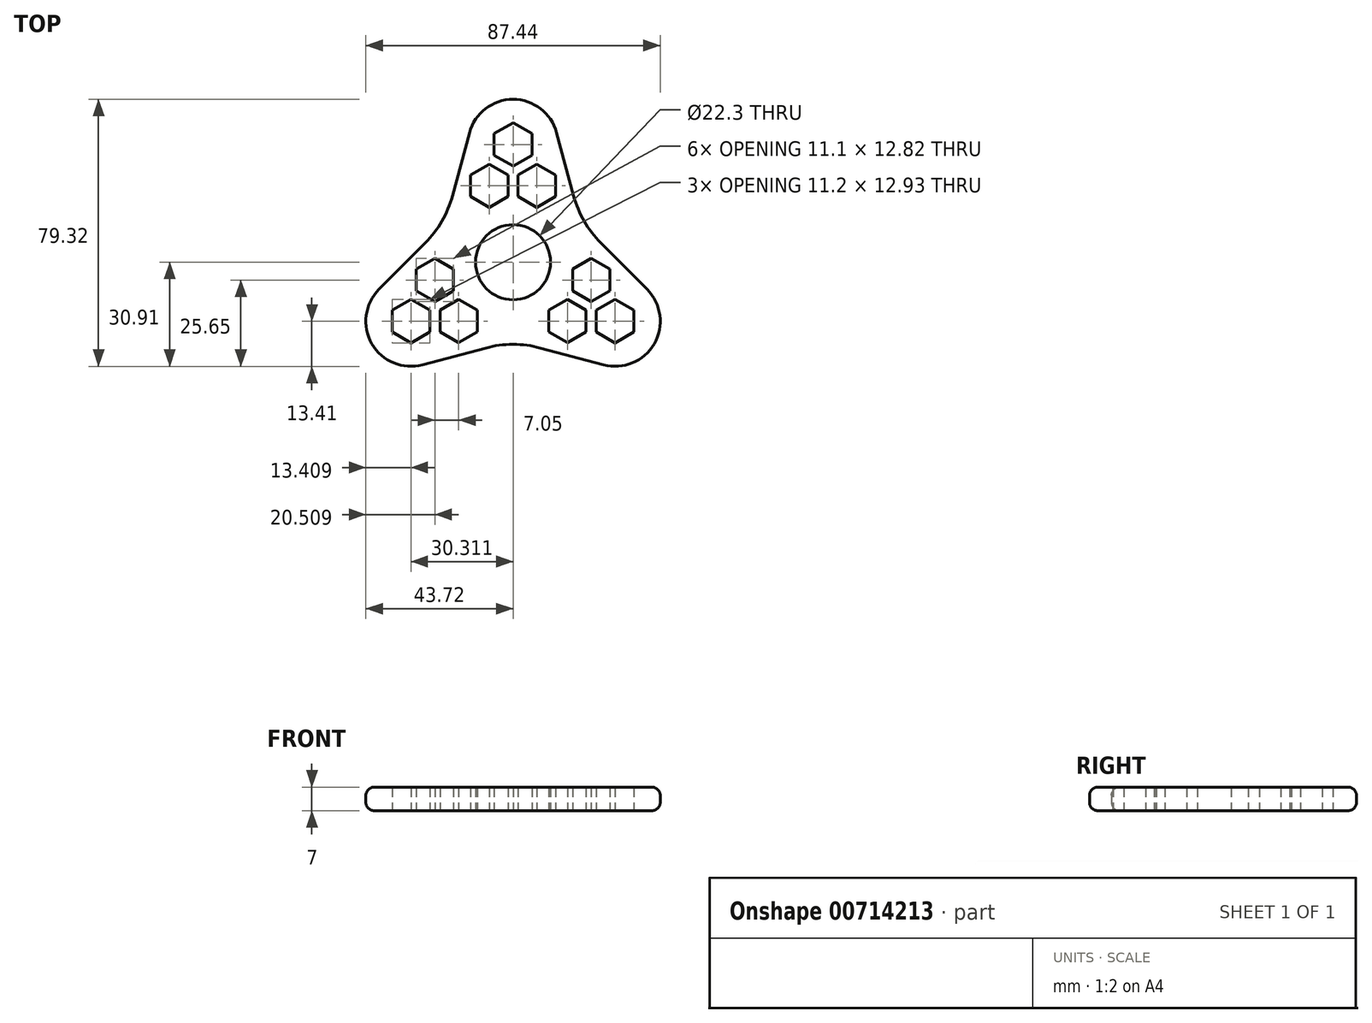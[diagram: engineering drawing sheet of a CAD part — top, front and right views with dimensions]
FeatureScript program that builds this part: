
annotation { "Feature Type Name" : "Feature", "Feature Type Description" : "" }
export const myFeature = defineFeature(function(context is Context, id is Id, definition is map)
    precondition{}
    {
        {
            var Q0;
            Q0=qCreatedBy(makeId("Top.planeOp"),FACE);
            var sketch = newSketch(context, id + "F0", { "sketchPlane" : qUnion([Q0])});
            skCircle(sketch, "E0", {"center": v(0, 0) * mm, "radius": 11.15 * mm});
            skCircle(sketch, "E1.cCircle", {"center": v(0, 35) * mm, "radius": 5.6 * mm, "construction": true});
            skLineSegment(sketch, "E1.0", {"start": v(5.6, 38.23) * mm, "end": v(5.6, 31.77) * mm});
            skLineSegment(sketch, "E1.1", {"start": v(5.6, 31.77) * mm, "end": v(0, 28.53) * mm});
            skLineSegment(sketch, "E1.2", {"start": v(0, 28.53) * mm, "end": v(-5.6, 31.77) * mm});
            skLineSegment(sketch, "E1.3", {"start": v(-5.6, 31.77) * mm, "end": v(-5.6, 38.23) * mm});
            skLineSegment(sketch, "E1.4", {"start": v(-5.6, 38.23) * mm, "end": v(0, 41.47) * mm});
            skLineSegment(sketch, "E1.5", {"start": v(0, 41.47) * mm, "end": v(5.6, 38.23) * mm});
            skPoint(sketch, "E1.0.midPoint", {"position": v(5.6, 35) * mm});
            skCircle(sketch, "E2.cCircle", {"center": v(-7.05, 22.73) * mm, "radius": 5.55 * mm, "construction": true});
            skLineSegment(sketch, "E2.0", {"start": v(-1.5, 25.94) * mm, "end": v(-1.5, 19.53) * mm});
            skLineSegment(sketch, "E2.1", {"start": v(-1.5, 19.53) * mm, "end": v(-7.05, 16.32) * mm});
            skLineSegment(sketch, "E2.2", {"start": v(-7.05, 16.32) * mm, "end": v(-12.6, 19.53) * mm});
            skLineSegment(sketch, "E2.3", {"start": v(-12.6, 19.53) * mm, "end": v(-12.6, 25.94) * mm});
            skLineSegment(sketch, "E2.4", {"start": v(-12.6, 25.94) * mm, "end": v(-7.05, 29.14) * mm});
            skLineSegment(sketch, "E2.5", {"start": v(-7.05, 29.14) * mm, "end": v(-1.5, 25.94) * mm});
            skPoint(sketch, "E2.0.midPoint", {"position": v(-1.5, 22.73) * mm});
            skCircle(sketch, "E3.cCircle", {"center": v(7.05, 22.73) * mm, "radius": 5.55 * mm, "construction": true});
            skLineSegment(sketch, "E3.0", {"start": v(12.6, 25.94) * mm, "end": v(12.6, 19.53) * mm});
            skLineSegment(sketch, "E3.1", {"start": v(12.6, 19.53) * mm, "end": v(7.05, 16.32) * mm});
            skLineSegment(sketch, "E3.2", {"start": v(7.05, 16.32) * mm, "end": v(1.5, 19.53) * mm});
            skLineSegment(sketch, "E3.3", {"start": v(1.5, 19.53) * mm, "end": v(1.5, 25.94) * mm});
            skLineSegment(sketch, "E3.4", {"start": v(1.5, 25.94) * mm, "end": v(7.05, 29.14) * mm});
            skLineSegment(sketch, "E3.5", {"start": v(7.05, 29.14) * mm, "end": v(12.6, 25.94) * mm});
            skPoint(sketch, "E3.0.midPoint", {"position": v(12.6, 22.73) * mm});
            skArc(sketch, "E4", {"start": v(-11.46, 19.36) * mm, "mid": v(-11.67, 19.24) * mm, "end": v(-11.88, 19.1) * mm});
            skArc(sketch, "E5", {"start": v(-10.76, 27) * mm, "mid": v(-10.73, 26.96) * mm, "end": v(-10.7, 26.92) * mm});
            skLineSegment(sketch, "E6", {"start": v(12.94, 38.48) * mm, "end": v(20.17, 11.64) * mm});
            skLineSegment(sketch, "E7", {"start": v(-12.94, 38.48) * mm, "end": v(-20.17, 11.64) * mm});
            skArc(sketch, "E8.trimOffspring", {"start": v(-1.6, 21.7) * mm, "mid": v(-1.55, 21.68) * mm, "end": v(-1.5, 21.68) * mm});
            skArc(sketch, "E9.trimOffspring", {"start": v(1.5, 21.68) * mm, "mid": v(1.55, 21.68) * mm, "end": v(1.6, 21.7) * mm});
            skArc(sketch, "E10.trimOffspring", {"start": v(12.94, 38.48) * mm, "mid": v(0, 48.4) * mm, "end": v(-12.94, 38.48) * mm});
            skArc(sketch, "E11.trimOffspring", {"start": v(10.7, 26.92) * mm, "mid": v(10.73, 26.96) * mm, "end": v(10.76, 27) * mm});
            skArc(sketch, "E12.trimOffspring", {"start": v(11.88, 19.1) * mm, "mid": v(11.67, 19.24) * mm, "end": v(11.46, 19.36) * mm});
            skArc(sketch, "E13.1.0", {"start": v(-39.8, -8.03) * mm, "mid": v(-41.92, -24.2) * mm, "end": v(-26.86, -30.45) * mm});
            skLineSegment(sketch, "E13.1.1", {"start": v(-39.8, -8.03) * mm, "end": v(-20.17, 11.64) * mm});
            skLineSegment(sketch, "E13.1.2", {"start": v(-26.86, -30.45) * mm, "end": v(0, -23.29) * mm});
            skLineSegment(sketch, "E13.1.3", {"start": v(-17.66, -2.06) * mm, "end": v(-17.66, -8.46) * mm});
            skLineSegment(sketch, "E13.1.4", {"start": v(-23.21, 1.15) * mm, "end": v(-17.66, -2.06) * mm});
            skLineSegment(sketch, "E13.1.5", {"start": v(-28.76, -2.06) * mm, "end": v(-23.21, 1.15) * mm});
            skLineSegment(sketch, "E13.1.6", {"start": v(-28.76, -8.46) * mm, "end": v(-28.76, -2.06) * mm});
            skLineSegment(sketch, "E13.1.7", {"start": v(-23.21, -11.67) * mm, "end": v(-28.76, -8.46) * mm});
            skLineSegment(sketch, "E13.1.8", {"start": v(-17.66, -8.46) * mm, "end": v(-23.21, -11.67) * mm});
            skLineSegment(sketch, "E13.1.9", {"start": v(-30.31, -11.03) * mm, "end": v(-24.71, -14.27) * mm});
            skLineSegment(sketch, "E13.1.10", {"start": v(-35.91, -14.27) * mm, "end": v(-30.31, -11.03) * mm});
            skLineSegment(sketch, "E13.1.11", {"start": v(-35.91, -20.73) * mm, "end": v(-35.91, -14.27) * mm});
            skLineSegment(sketch, "E13.1.12", {"start": v(-30.31, -23.97) * mm, "end": v(-35.91, -20.73) * mm});
            skLineSegment(sketch, "E13.1.13", {"start": v(-24.71, -20.73) * mm, "end": v(-30.31, -23.97) * mm});
            skLineSegment(sketch, "E13.1.14", {"start": v(-24.71, -14.27) * mm, "end": v(-24.71, -20.73) * mm});
            skLineSegment(sketch, "E13.1.15", {"start": v(-21.71, -20.68) * mm, "end": v(-21.71, -14.27) * mm});
            skLineSegment(sketch, "E13.1.16", {"start": v(-21.71, -14.27) * mm, "end": v(-16.16, -11.06) * mm});
            skLineSegment(sketch, "E13.1.17", {"start": v(-16.16, -11.06) * mm, "end": v(-10.61, -14.27) * mm});
            skLineSegment(sketch, "E13.1.18", {"start": v(-10.61, -14.27) * mm, "end": v(-10.61, -20.68) * mm});
            skLineSegment(sketch, "E13.1.19", {"start": v(-10.61, -20.68) * mm, "end": v(-16.16, -23.88) * mm});
            skLineSegment(sketch, "E13.1.20", {"start": v(-16.16, -23.88) * mm, "end": v(-21.71, -20.68) * mm});
            skArc(sketch, "E13.2.0", {"start": v(26.86, -30.45) * mm, "mid": v(41.92, -24.2) * mm, "end": v(39.8, -8.03) * mm});
            skLineSegment(sketch, "E13.2.1", {"start": v(26.86, -30.45) * mm, "end": v(0, -23.29) * mm});
            skLineSegment(sketch, "E13.2.2", {"start": v(39.8, -8.03) * mm, "end": v(20.17, 11.64) * mm});
            skLineSegment(sketch, "E13.2.3", {"start": v(10.61, -14.27) * mm, "end": v(16.16, -11.06) * mm});
            skLineSegment(sketch, "E13.2.4", {"start": v(10.61, -20.68) * mm, "end": v(10.61, -14.27) * mm});
            skLineSegment(sketch, "E13.2.5", {"start": v(16.16, -23.88) * mm, "end": v(10.61, -20.68) * mm});
            skLineSegment(sketch, "E13.2.6", {"start": v(21.71, -20.68) * mm, "end": v(16.16, -23.88) * mm});
            skLineSegment(sketch, "E13.2.7", {"start": v(21.71, -14.27) * mm, "end": v(21.71, -20.68) * mm});
            skLineSegment(sketch, "E13.2.8", {"start": v(16.16, -11.06) * mm, "end": v(21.71, -14.27) * mm});
            skLineSegment(sketch, "E13.2.9", {"start": v(24.71, -20.73) * mm, "end": v(24.71, -14.27) * mm});
            skLineSegment(sketch, "E13.2.10", {"start": v(30.31, -23.97) * mm, "end": v(24.71, -20.73) * mm});
            skLineSegment(sketch, "E13.2.11", {"start": v(35.91, -20.73) * mm, "end": v(30.31, -23.97) * mm});
            skLineSegment(sketch, "E13.2.12", {"start": v(35.91, -14.27) * mm, "end": v(35.91, -20.73) * mm});
            skLineSegment(sketch, "E13.2.13", {"start": v(30.31, -11.03) * mm, "end": v(35.91, -14.27) * mm});
            skLineSegment(sketch, "E13.2.14", {"start": v(24.71, -14.27) * mm, "end": v(30.31, -11.03) * mm});
            skLineSegment(sketch, "E13.2.15", {"start": v(28.76, -8.46) * mm, "end": v(23.21, -11.67) * mm});
            skLineSegment(sketch, "E13.2.16", {"start": v(23.21, -11.67) * mm, "end": v(17.66, -8.46) * mm});
            skLineSegment(sketch, "E13.2.17", {"start": v(17.66, -8.46) * mm, "end": v(17.66, -2.06) * mm});
            skLineSegment(sketch, "E13.2.18", {"start": v(17.66, -2.06) * mm, "end": v(23.21, 1.15) * mm});
            skLineSegment(sketch, "E13.2.19", {"start": v(23.21, 1.15) * mm, "end": v(28.76, -2.06) * mm});
            skLineSegment(sketch, "E13.2.20", {"start": v(28.76, -2.06) * mm, "end": v(28.76, -8.46) * mm});
            skPoint(sketch, "E14.orphan", {"position": v(-15.93, 15.9) * mm});
            skPoint(sketch, "E15.orphan", {"position": v(-21.73, 5.85) * mm});
            skPoint(sketch, "E16.orphan", {"position": v(-5.8, -21.74) * mm});
            skPoint(sketch, "E17.orphan", {"position": v(5.8, -21.74) * mm});
            skPoint(sketch, "E18.orphan", {"position": v(21.73, 5.85) * mm});
            skPoint(sketch, "E19.orphan", {"position": v(15.93, 15.9) * mm});
            skSolve(sketch);
        }
        {
            var Q0;
            Q0 = qSketchRegion(id + "F0", true);
            extrude(context, id + "F1", {"entities" : qUnion([Q0]), "depth" : 7 * mm, "offsetDistance" : 25 * mm});
        }
        {
            var Q0;
            Q0=makeQuery(id+"F1.opExtrude","SWEPT_EDGE",EDGE,{"disambiguationData":[OSD([sQuery(id+"F0.wireOp",EDGE,"E6"),sQuery(id+"F0.wireOp",EDGE,"E13.2.2")])]});
            var Q1;
            Q1=makeQuery(id+"F1.opExtrude","SWEPT_EDGE",EDGE,{"disambiguationData":[OSD([sQuery(id+"F0.wireOp",EDGE,"E7"),sQuery(id+"F0.wireOp",EDGE,"E13.1.1")])]});
            var Q2;
            Q2=makeQuery(id+"F1.opExtrude","SWEPT_EDGE",EDGE,{"disambiguationData":[OSD([sQuery(id+"F0.wireOp",EDGE,"E13.1.2"),sQuery(id+"F0.wireOp",EDGE,"E13.2.1")])]});
            fillet(context, id + "F2", {"entities" : qUnion([Q0, Q1, Q2]), "radius" : 31.45 * mm, "tangentPropagation" : true, "allowEdgeOverflow" : false});
        }
        {
            var Q0;
            Q0=makeQuery(id+"F1.opExtrude","CAP_EDGE",EDGE,{"disambiguationData":[OSD([sQuery(id+"F0.wireOp",EDGE,"E13.1.1")])],"isStart":false});
            var Q1;
            {var subQ0=sQuery(id+"F0.wireOp",EDGE,"E13.1.1");var subQ1=sQuery(id+"F0.wireOp",EDGE,"E7");Q1=makeQuery(id+"F2.opFillet","BLEND_EDGE",EDGE,{"blendedFrom":[makeQuery(id+"F1.opExtrude","SWEPT_EDGE",EDGE,{"disambiguationData":[OSD([subQ1,subQ0])]}),makeQuery(id+"F1.opExtrude","CAP_FACE",FACE,{"disambiguationData":[OSD([sQuery(id+"F0.wireOp",EDGE,"E0"),sQuery(id+"F0.wireOp",EDGE,"E1.0"),sQuery(id+"F0.wireOp",EDGE,"E1.1"),sQuery(id+"F0.wireOp",EDGE,"E1.2"),sQuery(id+"F0.wireOp",EDGE,"E1.3"),sQuery(id+"F0.wireOp",EDGE,"E1.4"),sQuery(id+"F0.wireOp",EDGE,"E1.5"),sQuery(id+"F0.wireOp",EDGE,"E2.0"),sQuery(id+"F0.wireOp",EDGE,"E2.1"),sQuery(id+"F0.wireOp",EDGE,"E2.2"),sQuery(id+"F0.wireOp",EDGE,"E2.3"),sQuery(id+"F0.wireOp",EDGE,"E2.4"),sQuery(id+"F0.wireOp",EDGE,"E2.5"),sQuery(id+"F0.wireOp",EDGE,"E3.0"),sQuery(id+"F0.wireOp",EDGE,"E3.1"),sQuery(id+"F0.wireOp",EDGE,"E3.2"),sQuery(id+"F0.wireOp",EDGE,"E3.3"),sQuery(id+"F0.wireOp",EDGE,"E3.4"),sQuery(id+"F0.wireOp",EDGE,"E3.5"),sQuery(id+"F0.wireOp",EDGE,"E6"),subQ1,sQuery(id+"F0.wireOp",EDGE,"E10.trimOffspring"),sQuery(id+"F0.wireOp",EDGE,"E13.1.0"),subQ0,sQuery(id+"F0.wireOp",EDGE,"E13.1.2"),sQuery(id+"F0.wireOp",EDGE,"E13.1.3"),sQuery(id+"F0.wireOp",EDGE,"E13.1.4"),sQuery(id+"F0.wireOp",EDGE,"E13.1.5"),sQuery(id+"F0.wireOp",EDGE,"E13.1.6"),sQuery(id+"F0.wireOp",EDGE,"E13.1.7"),sQuery(id+"F0.wireOp",EDGE,"E13.1.8"),sQuery(id+"F0.wireOp",EDGE,"E13.1.9"),sQuery(id+"F0.wireOp",EDGE,"E13.1.10"),sQuery(id+"F0.wireOp",EDGE,"E13.1.11"),sQuery(id+"F0.wireOp",EDGE,"E13.1.12"),sQuery(id+"F0.wireOp",EDGE,"E13.1.13"),sQuery(id+"F0.wireOp",EDGE,"E13.1.14"),sQuery(id+"F0.wireOp",EDGE,"E13.1.15"),sQuery(id+"F0.wireOp",EDGE,"E13.1.16"),sQuery(id+"F0.wireOp",EDGE,"E13.1.17"),sQuery(id+"F0.wireOp",EDGE,"E13.1.18"),sQuery(id+"F0.wireOp",EDGE,"E13.1.19"),sQuery(id+"F0.wireOp",EDGE,"E13.1.20"),sQuery(id+"F0.wireOp",EDGE,"E13.2.0"),sQuery(id+"F0.wireOp",EDGE,"E13.2.1"),sQuery(id+"F0.wireOp",EDGE,"E13.2.2"),sQuery(id+"F0.wireOp",EDGE,"E13.2.3"),sQuery(id+"F0.wireOp",EDGE,"E13.2.4"),sQuery(id+"F0.wireOp",EDGE,"E13.2.5"),sQuery(id+"F0.wireOp",EDGE,"E13.2.6"),sQuery(id+"F0.wireOp",EDGE,"E13.2.7"),sQuery(id+"F0.wireOp",EDGE,"E13.2.8"),sQuery(id+"F0.wireOp",EDGE,"E13.2.9"),sQuery(id+"F0.wireOp",EDGE,"E13.2.10"),sQuery(id+"F0.wireOp",EDGE,"E13.2.11"),sQuery(id+"F0.wireOp",EDGE,"E13.2.12"),sQuery(id+"F0.wireOp",EDGE,"E13.2.13"),sQuery(id+"F0.wireOp",EDGE,"E13.2.14"),sQuery(id+"F0.wireOp",EDGE,"E13.2.15"),sQuery(id+"F0.wireOp",EDGE,"E13.2.16"),sQuery(id+"F0.wireOp",EDGE,"E13.2.17"),sQuery(id+"F0.wireOp",EDGE,"E13.2.18"),sQuery(id+"F0.wireOp",EDGE,"E13.2.19"),sQuery(id+"F0.wireOp",EDGE,"E13.2.20")])],"isStart":true})],"blendedInto":[makeQuery(id+"F1.opExtrude","CAP_FACE",FACE,{"disambiguationData":[OSD([sQuery(id+"F0.wireOp",EDGE,"E0"),sQuery(id+"F0.wireOp",EDGE,"E1.0"),sQuery(id+"F0.wireOp",EDGE,"E1.1"),sQuery(id+"F0.wireOp",EDGE,"E1.2"),sQuery(id+"F0.wireOp",EDGE,"E1.3"),sQuery(id+"F0.wireOp",EDGE,"E1.4"),sQuery(id+"F0.wireOp",EDGE,"E1.5"),sQuery(id+"F0.wireOp",EDGE,"E2.0"),sQuery(id+"F0.wireOp",EDGE,"E2.1"),sQuery(id+"F0.wireOp",EDGE,"E2.2"),sQuery(id+"F0.wireOp",EDGE,"E2.3"),sQuery(id+"F0.wireOp",EDGE,"E2.4"),sQuery(id+"F0.wireOp",EDGE,"E2.5"),sQuery(id+"F0.wireOp",EDGE,"E3.0"),sQuery(id+"F0.wireOp",EDGE,"E3.1"),sQuery(id+"F0.wireOp",EDGE,"E3.2"),sQuery(id+"F0.wireOp",EDGE,"E3.3"),sQuery(id+"F0.wireOp",EDGE,"E3.4"),sQuery(id+"F0.wireOp",EDGE,"E3.5"),sQuery(id+"F0.wireOp",EDGE,"E6"),subQ1,sQuery(id+"F0.wireOp",EDGE,"E10.trimOffspring"),sQuery(id+"F0.wireOp",EDGE,"E13.1.0"),subQ0,sQuery(id+"F0.wireOp",EDGE,"E13.1.2"),sQuery(id+"F0.wireOp",EDGE,"E13.1.3"),sQuery(id+"F0.wireOp",EDGE,"E13.1.4"),sQuery(id+"F0.wireOp",EDGE,"E13.1.5"),sQuery(id+"F0.wireOp",EDGE,"E13.1.6"),sQuery(id+"F0.wireOp",EDGE,"E13.1.7"),sQuery(id+"F0.wireOp",EDGE,"E13.1.8"),sQuery(id+"F0.wireOp",EDGE,"E13.1.9"),sQuery(id+"F0.wireOp",EDGE,"E13.1.10"),sQuery(id+"F0.wireOp",EDGE,"E13.1.11"),sQuery(id+"F0.wireOp",EDGE,"E13.1.12"),sQuery(id+"F0.wireOp",EDGE,"E13.1.13"),sQuery(id+"F0.wireOp",EDGE,"E13.1.14"),sQuery(id+"F0.wireOp",EDGE,"E13.1.15"),sQuery(id+"F0.wireOp",EDGE,"E13.1.16"),sQuery(id+"F0.wireOp",EDGE,"E13.1.17"),sQuery(id+"F0.wireOp",EDGE,"E13.1.18"),sQuery(id+"F0.wireOp",EDGE,"E13.1.19"),sQuery(id+"F0.wireOp",EDGE,"E13.1.20"),sQuery(id+"F0.wireOp",EDGE,"E13.2.0"),sQuery(id+"F0.wireOp",EDGE,"E13.2.1"),sQuery(id+"F0.wireOp",EDGE,"E13.2.2"),sQuery(id+"F0.wireOp",EDGE,"E13.2.3"),sQuery(id+"F0.wireOp",EDGE,"E13.2.4"),sQuery(id+"F0.wireOp",EDGE,"E13.2.5"),sQuery(id+"F0.wireOp",EDGE,"E13.2.6"),sQuery(id+"F0.wireOp",EDGE,"E13.2.7"),sQuery(id+"F0.wireOp",EDGE,"E13.2.8"),sQuery(id+"F0.wireOp",EDGE,"E13.2.9"),sQuery(id+"F0.wireOp",EDGE,"E13.2.10"),sQuery(id+"F0.wireOp",EDGE,"E13.2.11"),sQuery(id+"F0.wireOp",EDGE,"E13.2.12"),sQuery(id+"F0.wireOp",EDGE,"E13.2.13"),sQuery(id+"F0.wireOp",EDGE,"E13.2.14"),sQuery(id+"F0.wireOp",EDGE,"E13.2.15"),sQuery(id+"F0.wireOp",EDGE,"E13.2.16"),sQuery(id+"F0.wireOp",EDGE,"E13.2.17"),sQuery(id+"F0.wireOp",EDGE,"E13.2.18"),sQuery(id+"F0.wireOp",EDGE,"E13.2.19"),sQuery(id+"F0.wireOp",EDGE,"E13.2.20")])],"isStart":true})]});}
            fillet(context, id + "F3", {"entities" : qUnion([Q0, Q1]), "radius" : 2.5 * mm, "tangentPropagation" : true, "allowEdgeOverflow" : false});
        }
    });
